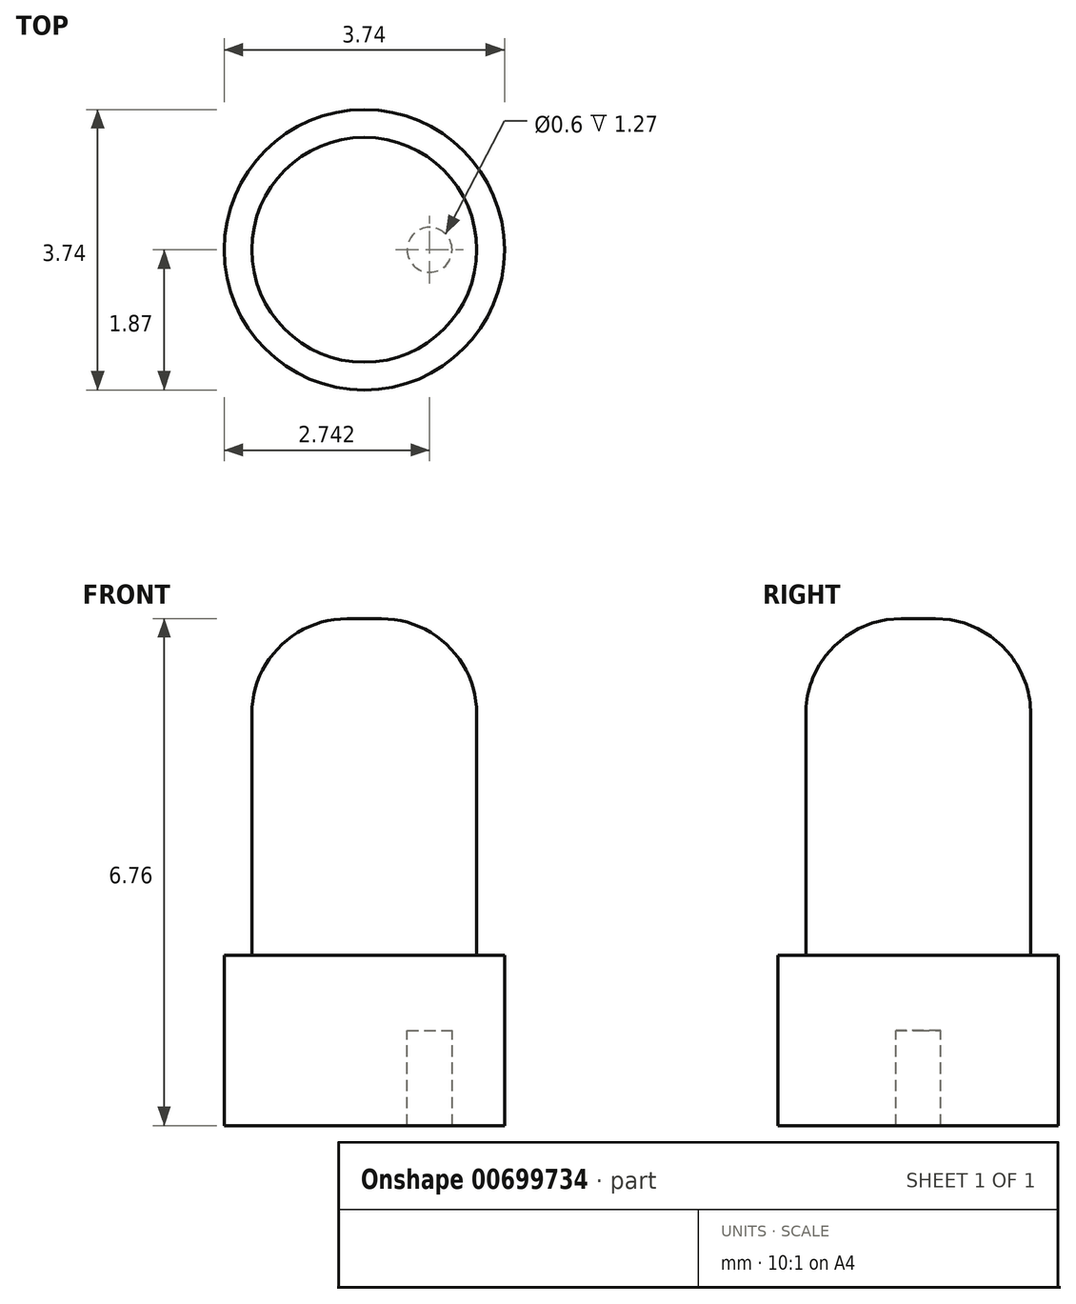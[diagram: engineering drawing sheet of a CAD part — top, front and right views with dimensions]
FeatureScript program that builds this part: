
annotation { "Feature Type Name" : "Feature", "Feature Type Description" : "" }
export const myFeature = defineFeature(function(context is Context, id is Id, definition is map)
    precondition{}
    {
        {
            var Q0;
            Q0=qCreatedBy(makeId("Front.planeOp"),FACE);
            var sketch = newSketch(context, id + "F0", { "sketchPlane" : qUnion([Q0])});
            skLineSegment(sketch, "E0", {"start": v(0, 0) * mm, "end": v(-1.87, 0) * mm});
            skLineSegment(sketch, "E1", {"start": v(-1.87, 0) * mm, "end": v(-1.87, 1) * mm});
            skLineSegment(sketch, "E2", {"start": v(-1.87, 1) * mm, "end": v(-1.5, 1) * mm});
            skLineSegment(sketch, "E3", {"start": v(-1.5, 1) * mm, "end": v(-1.5, 4.22) * mm});
            skLineSegment(sketch, "E4", {"start": v(-0.23, 5.49) * mm, "end": v(0, 5.49) * mm});
            skLineSegment(sketch, "E5", {"start": v(0, 5.49) * mm, "end": v(0, 0) * mm});
            skPoint(sketch, "E6.visualSharp", {"position": v(-1.5, 5.49) * mm});
            skArc(sketch, "E6.filletArc", {"start": v(-0.23, 5.49) * mm, "mid": v(-1.13, 5.12) * mm, "end": v(-1.5, 4.22) * mm});
            skSolve(sketch);
        }
        {
            var Q0;
            Q0=makeQuery(id+"F0.imprint","IMPRINT",FACE,{"disambiguationData":[TD([[makeQuery(id+"F0.imprint","IMPRINT",EDGE,{"derivedFrom":sQuery(id+"F0.wireOp",EDGE,"E0")}),-1.0]])]});
            var Q1;
            Q1=sQuery(id+"F0.wireOp",EDGE,"E5");
            revolve(context, id + "F1", {"entities" : qUnion([Q0]), "axis" : qUnion([Q1]), "revolveType" : RevolveType.FULL});
        }
        {
            var Q0;
            Q0=makeQuery(id+"F1.opRevolve","SWEPT_FACE",FACE,{"disambiguationData":[OSD([sQuery(id+"F0.wireOp",EDGE,"E0")])]});
            var sketch = newSketch(context, id + "F2", { "sketchPlane" : qUnion([Q0])});
            skCircle(sketch, "E7", {"center": v(-0.87, 0) * mm, "radius": 0.3 * mm});
            skLineSegment(sketch, "E8", {"start": v(0, 1.87) * mm, "end": v(0, 0) * mm, "construction": true});
            skLineSegment(sketch, "E9", {"start": v(0, -1.87) * mm, "end": v(0, 0) * mm, "construction": true});
            skCircle(sketch, "E10.MirrorC", {"center": v(0.87, 0) * mm, "radius": 0.3 * mm});
            skSolve(sketch);
        }
        {
            var Q0;
            Q0=makeQuery(id+"F2.imprint","IMPRINT",FACE,{"disambiguationData":[TD([[makeQuery(id+"F2.imprint","IMPRINT",EDGE,{"derivedFrom":sQuery(id+"F2.wireOp",EDGE,"E7")}),1.0]])]});
            var Q1;
            Q1=makeQuery(id+"F2.imprint","IMPRINT",FACE,{"disambiguationData":[TD([[makeQuery(id+"F2.imprint","IMPRINT",EDGE,{"derivedFrom":sQuery(id+"F2.wireOp",EDGE,"75Fwa33Y-8WvS-vZQn-WcMw-DsbDLF67jLZr")}),1.0]])]});
            var Q2;
            Q2=makeQuery(id+"F2.imprint","IMPRINT",FACE,{"disambiguationData":[TD([[makeQuery(id+"F2.imprint","IMPRINT",EDGE,{"derivedFrom":sQuery(id+"F2.wireOp",EDGE,"E10.MirrorC")}),-1.0]])]});
            extrude(context, id + "F3", {"entities" : qUnion([Q0, Q1, Q2]), "operationType" : NewBodyOperationType.ADD, "depth" : 1.27 * mm, "offsetDistance" : 25.4 * mm});
        }
    });
